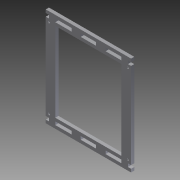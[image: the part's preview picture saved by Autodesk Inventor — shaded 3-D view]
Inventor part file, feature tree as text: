
AUTODESK INVENTOR PART (.ipt)
format: ipt  version: 2011 (Build 150239000, 239)  size: 257,024 bytes
history: native  units: in
note: dims shown in document units (in); Inventor stores cm internally (conversion verified against a paired STEP export)
features: extrude x6, sketch x6
ambient origin geometry x8: Origin, YZ Plane, XZ Plane, XY Plane, X Axis, Y Axis, Z Axis, Center Point
bodies: Solid1 (feature_tree)
feature tree (12):
  extrude  "Extrusion1"  Depth=6.75in
  extrude  "Extrusion2"  Depth=0.5in
  extrude  "Extrusion3"  Depth=0.5in
  extrude  "Extrusion4"  Depth=5.75in
  extrude  "Extrusion5"  Depth=0.5in
  extrude  "Extrusion6"  Depth=1.5in
  sketch  "Sketch1"  dims[d0=5.2in d1=6.75in]
  sketch  "Sketch2"  dims[d2=0.25in d3=0.5in]
  sketch  "Sketch3"  dims[d4=5.7in d5=0.5in]
  sketch  "Sketch4"  dims[d6=0.5in d7=5.75in]
  sketch  "Sketch5"  dims[d8=0.375in d9=0.5in]
  sketch  "Sketch6"  dims[d10=0.25in d11=1.5in d12=0.25in d13=1.5in d14=0.25in d15=0.156in d16=0.156in d17=0.25in d18=0.0in d19=0.125in d20=0.0in d21=0.25in d22=0.0in d23=0.25in d24=0.0in d25=0.25in d26=0.0in d27=0.25in d28=0.25in d29=0.25in d30=0.25in d31=0.25in d32=0.25in d33=0.0in]
